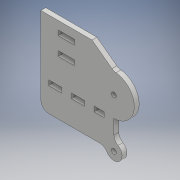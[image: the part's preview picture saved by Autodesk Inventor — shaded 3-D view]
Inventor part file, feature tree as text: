
AUTODESK INVENTOR PART (.ipt)
format: ipt  version: 2018 (Build 220112000, 112)  size: 145,920 bytes
history: native  units: mm
features: other x1, extrude x1, sketch x1
ambient origin geometry x8: Origin, YZ Plane, XZ Plane, XY Plane, X Axis, Y Axis, Z Axis, Center Point
bodies: Body1 (feature_tree)
feature tree (3):
  other  "Sólido1"
  extrude  "Extrusión1"  Depth=16.0mm
  sketch  "Boceto1"  dims[d26=30.0mm d125=16.0mm d165=8.0mm d166=6.0mm d167=8.0mm d169=6.0mm d170=5.0mm d172=3.0mm d173=0.0mm]
